# Revit family: Hager-Univers-IP44-D205-H800-Cl.I-encl-NoHosted-DE-de
name_source: partatom
category: Equipement électrique
units: mm (PartAtom-declared; Revit-internal decimal feet)

## family parameters
Basée sur le plan de construction = Oui
Configuration du panneau = Deux colonnes, circuits au sein
Cote de connecteur circulaire = Utiliser le diamètre
Couper avec des vides une fois chargée = Non
Partagée = Non
Point de calcul de pièce = Non
Toujours verticalement = Oui
Type d'élément = Tableau de raccordement

## types (10) — shared parameters
Commentaires du type = Univers
EF000003 - Montageart = EV000384 - Aufputz
EF000007 - Farbe = EV000202 - weiß
EF000040 - Höhe = 800 mm  [stored 2.62467 ft]
EF000049 - Tiefe = 205 mm  [stored 0.672572 ft]
EF000116 - RAL-Nummer = 9010
EF000118 - Mit Montageplatte = Non
EF000218 - Einbautiefe = 205 mm  [stored 0.672572 ft]
EF000266 - Anzahl der Reihen = 5
EF000339 - Art der Abdeckung = EV001012 - Deckel
EF001088 - Anbaumöglichkeit = Oui
EF001131 - Innentiefe = 205 mm  [stored 0.672572 ft]
EF001596 - Werkstoff des Gehäuses = EV000179 - Stahl
EF001613 - Funktionserhalt = EV000494 - ohne
EF003532 - Geeignet für Außengebrauch = Non
EF004293 - Schlagfestigkeit = EV006815 - IK09
EF005474 - Schutzart (IP) = EV006418 - IP44
EF006244 - Transparenter Deckel/Tür = Non
EF006306 - Mit Schloss = Non
EF007800 - Geeignet für Blitzschutz = Non
EF008873 - Nennstrom (In) = 250 A
EF009170 - Materialstärke Gehäuse = 1 mm  [stored 0.00328084 ft]
EF009171 - Materialstärke Tür/Deckel = 1 mm  [stored 0.00328084 ft]
EF009212 - Ausführung Deckel = EV000116 - geschlossen
EF015940 - Deckel mit Überdruckentlastung = Non
Elévation par défaut = 1219 mm
Fabricant = Hager
HG000002 - Mit tür = Oui
HG000003 - Bereich = Univers
HG000006 - Unterputz = Non
HG000023 - Gehäuse mit doppeltem Querschnitt = Non
HG000024 - Höhe des unteren Teils = 600 mm
HG000026 - Stehend auf dem Boden = Non
zero-valued in all types: HG000027 - Sockelhöhe

## per-type parameters (varying)
| type | EF000008 - Breite | EF000437 - Anzahl der Leitungseinführungen | EF002950 - Breite in Teilungseinheiten | EF004427 - Anzahl der Module | EF004464 - Art der Tür | EF009554 - Anzahl der Öffnungen für Flanschplatten | HG000004 - Herstellerreferenz | HG000009 - Doppelflügeligen Tür | HG000010 - Asymmetrische Türen |
| Aufputz IP44 B1050 H800 T205  - FP54TN2 | 1050 mm | 8 | 48 | 240 | EV003602 - Doppel | 8 | FP54TN2 | Oui | Non |
| Aufputz IP44 B1300 H800 T205  - FP55TN | 1300 mm  [stored 4.26509 ft] | 10 | 60 | 300 | EV003602 - Doppel | 10 | FP55TN | Non | Non |
| Aufputz IP44 B1300 H800 T205  - FP55TN2 | 1300 mm  [stored 4.26509 ft] | 10 | 60 | 300 | EV003602 - Doppel | 10 | FP55TN2 | Oui | Oui |
| Aufputz IP44 B300 H800 T205  - FP51TN | 300 mm | 2 | 12 | 60 | EV002646 - Einzel | 2 | FP51TN | Non | Non |
| Aufputz IP44 B300 H800 T205  - FP51TN2 | 300 mm | 2 | 12 | 60 | EV002646 - Einzel | 2 | FP51TN2 | Non | Non |
| Aufputz IP44 B300 H800 T205  - FP51TW | 300 mm | 2 | 12 | 60 | EV002646 - Einzel | 2 | FP51TW | Non | Non |
| Aufputz IP44 B550 H800 T205  - FP52TN | 550 mm | 4 | 24 | 120 | EV002646 - Einzel | 4 | FP52TN | Non | Non |
| Aufputz IP44 B550 H800 T205  - FP52TN2 | 550 mm | 4 | 24 | 120 | EV002646 - Einzel | 4 | FP52TN2 | Non | Non |
| Aufputz IP44 B800 H800 T205  - FP53TN | 800 mm  [stored 2.62467 ft] | 6 | 36 | 180 | EV002646 - Einzel | 6 | FP53TN | Non | Non |
| Aufputz IP44 B800 H800 T205  - FP53TN2 | 800 mm  [stored 2.62467 ft] | 6 | 36 | 180 | EV002646 - Einzel | 6 | FP53TN2 | Non | Non |

note: [stored X ft] marks values corroborated as IEEE doubles in the binary element streams (Revit-internal decimal feet)

## geometry (parser evidence)
native form markers: Blend x4, Sweep x11
no freeform markers — native parametric forms only
